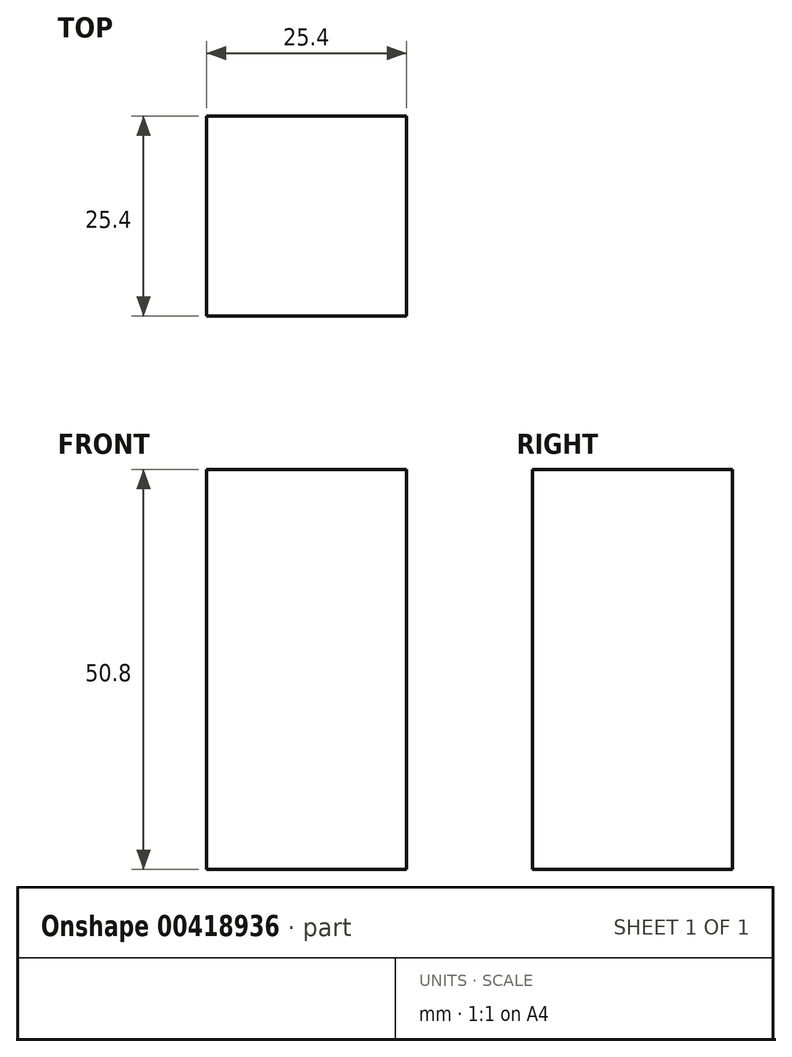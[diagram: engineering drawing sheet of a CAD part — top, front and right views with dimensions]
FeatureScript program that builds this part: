
annotation { "Feature Type Name" : "Feature", "Feature Type Description" : "" }
export const myFeature = defineFeature(function(context is Context, id is Id, definition is map)
    precondition{}
    {
        {
            var Q0;
            Q0=qCreatedBy(makeId("Front.planeOp"),FACE);
            var sketch = newSketch(context, id + "F0", { "sketchPlane" : qUnion([Q0])});
            skLineSegment(sketch, "E0.bottom", {"start": v(-20.05, -1.72) * mm, "end": v(-45.45, -1.72) * mm});
            skLineSegment(sketch, "E0.top", {"start": v(-20.05, 49.08) * mm, "end": v(-45.45, 49.08) * mm});
            skLineSegment(sketch, "E0.left", {"start": v(-20.05, -1.72) * mm, "end": v(-20.05, 49.08) * mm});
            skLineSegment(sketch, "E0.right", {"start": v(-45.45, -1.72) * mm, "end": v(-45.45, 49.08) * mm});
            skSolve(sketch);
        }
        {
            var Q0;
            Q0 = qSketchRegion(id + "F0", true);
            extrude(context, id + "F1", {"entities" : qUnion([Q0]), "depth" : 25.4 * mm});
        }
        {
            var Q0;
            Q0=qCreatedBy(makeId("Front.planeOp"),FACE);
            var sketch = newSketch(context, id + "F2", { "sketchPlane" : qUnion([Q0])});
            skLineSegment(sketch, "E1.bottom", {"start": v(-45.07, 0) * mm, "end": v(-19.67, 0) * mm});
            skLineSegment(sketch, "E1.top", {"start": v(-45.07, 25.4) * mm, "end": v(-19.67, 25.4) * mm});
            skLineSegment(sketch, "E1.left", {"start": v(-45.07, 0) * mm, "end": v(-45.07, 25.4) * mm});
            skLineSegment(sketch, "E1.right", {"start": v(-19.67, 0) * mm, "end": v(-19.67, 25.4) * mm});
            skSolve(sketch);
        }
        {
            var Q0;
            Q0 = qSketchRegion(id + "F2", true);
            extrude(context, id + "F3", {"entities" : qUnion([Q0]), "operationType" : NewBodyOperationType.REMOVE, "oppositeDirection" : true, "depth" : 25.4 * mm});
        }
    });
